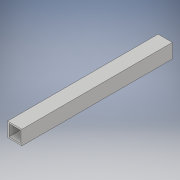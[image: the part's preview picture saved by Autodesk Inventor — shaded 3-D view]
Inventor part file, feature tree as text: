
AUTODESK INVENTOR PART (.ipt)
format: ipt  version: 2018 (Build 220112000, 112)  size: 98,304 bytes
history: native  units: in
note: dims shown in document units (in); Inventor stores cm internally (conversion verified against a paired STEP export)
features: extrude x1, sketch x1
ambient origin geometry x8: Origin, YZ Plane, XZ Plane, XY Plane, X Axis, Y Axis, Z Axis, Center Point
bodies: Solid1 (feature_tree)
feature tree (2):
  extrude  "Extrusion1"  Depth=1.0in
  sketch  "Sketch1"  dims[d0=1.0in d1=1.0in d2=0.1in d3=0.1in d4=10.5in d5=0.0in]
